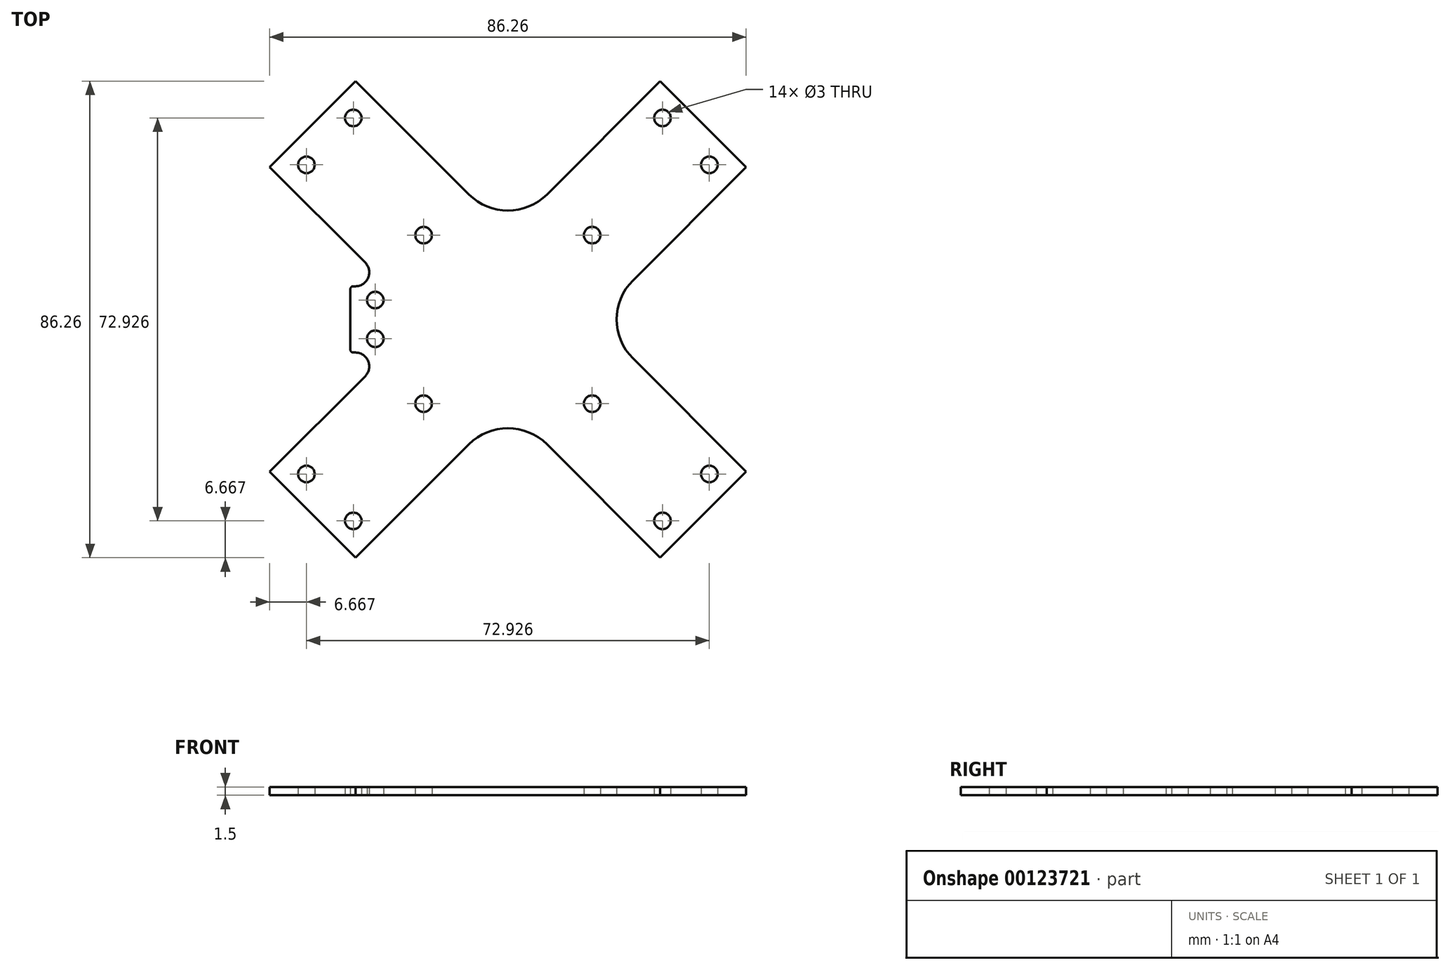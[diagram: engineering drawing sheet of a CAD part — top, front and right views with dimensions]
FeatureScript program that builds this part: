
annotation { "Feature Type Name" : "Feature", "Feature Type Description" : "" }
export const myFeature = defineFeature(function(context is Context, id is Id, definition is map)
    precondition{}
    {
        {
            var Q0;
            Q0=qCreatedBy(makeId("Top.planeOp"),FACE);
            var sketch = newSketch(context, id + "F0", { "sketchPlane" : qUnion([Q0])});
            skLineSegment(sketch, "E0", {"start": v(-42.43, -42.43) * mm, "end": v(42.43, 42.43) * mm, "construction": true});
            skLineSegment(sketch, "E1", {"start": v(-42.43, 42.43) * mm, "end": v(42.43, -42.43) * mm, "construction": true});
            skCircle(sketch, "E2", {"center": v(-15.25, 15.25) * mm, "radius": 1.5 * mm});
            skCircle(sketch, "E3.0.1.0", {"center": v(-15.25, -15.25) * mm, "radius": 1.5 * mm});
            skCircle(sketch, "E3.1.0.0", {"center": v(15.25, 15.25) * mm, "radius": 1.5 * mm});
            skCircle(sketch, "E3.1.1.0", {"center": v(15.25, -15.25) * mm, "radius": 1.5 * mm});
            skLineSegment(sketch, "E3.1.1.1", {"start": v(14.19, -14.19) * mm, "end": v(72.93, -72.93) * mm, "construction": true});
            skLineSegment(sketch, "E3.direction1", {"start": v(-15.25, 15.25) * mm, "end": v(15.25, 15.25) * mm, "construction": true});
            skLineSegment(sketch, "E3.direction2", {"start": v(-15.25, 15.25) * mm, "end": v(-15.25, -15.25) * mm, "construction": true});
            skLineSegment(sketch, "E4", {"start": v(-36.46, 27.98) * mm, "end": v(-27.98, 36.46) * mm, "construction": true});
            skLineSegment(sketch, "E5", {"start": v(27.98, 36.46) * mm, "end": v(36.46, 27.98) * mm, "construction": true});
            skLineSegment(sketch, "E6", {"start": v(27.98, -36.46) * mm, "end": v(36.46, -27.98) * mm, "construction": true});
            skLineSegment(sketch, "E7", {"start": v(-36.46, -27.98) * mm, "end": v(-27.98, -36.46) * mm, "construction": true});
            skCircle(sketch, "E8", {"center": v(-36.46, 27.98) * mm, "radius": 1.5 * mm});
            skCircle(sketch, "E9", {"center": v(-27.98, 36.46) * mm, "radius": 1.5 * mm});
            skCircle(sketch, "E10", {"center": v(27.98, 36.46) * mm, "radius": 1.5 * mm});
            skCircle(sketch, "E11", {"center": v(36.46, 27.98) * mm, "radius": 1.5 * mm});
            skCircle(sketch, "E12", {"center": v(36.46, -27.98) * mm, "radius": 1.5 * mm});
            skCircle(sketch, "E13", {"center": v(27.98, -36.46) * mm, "radius": 1.5 * mm});
            skCircle(sketch, "E14", {"center": v(-27.98, -36.46) * mm, "radius": 1.5 * mm});
            skCircle(sketch, "E15", {"center": v(-36.46, -27.98) * mm, "radius": 1.5 * mm});
            skLineSegment(sketch, "E16", {"start": v(-43.13, 27.58) * mm, "end": v(-27.58, 43.13) * mm});
            skLineSegment(sketch, "E17", {"start": v(27.58, 43.13) * mm, "end": v(43.13, 27.58) * mm});
            skLineSegment(sketch, "E18", {"start": v(27.58, -43.13) * mm, "end": v(43.13, -27.58) * mm});
            skLineSegment(sketch, "E19", {"start": v(-43.13, -27.58) * mm, "end": v(-27.58, -43.13) * mm});
            skPoint(sketch, "E20.endSnap0", {"position": v(-15.25, 0) * mm});
            skLineSegment(sketch, "E21", {"start": v(-43.13, 27.58) * mm, "end": v(-25.82, 10.27) * mm});
            skLineSegment(sketch, "E22", {"start": v(-27.58, 43.13) * mm, "end": v(-7.07, 22.63) * mm});
            skLineSegment(sketch, "E23", {"start": v(-43.13, -27.58) * mm, "end": v(-25.82, -10.27) * mm});
            skLineSegment(sketch, "E24", {"start": v(-27.58, -43.13) * mm, "end": v(-7.07, -22.63) * mm});
            skLineSegment(sketch, "E25.trimOffspring", {"start": v(7.07, -22.63) * mm, "end": v(27.58, -43.13) * mm});
            skLineSegment(sketch, "E26.trimOffspring", {"start": v(22.63, 7.07) * mm, "end": v(43.13, 27.58) * mm});
            skLineSegment(sketch, "E27.trimOffspring", {"start": v(22.63, -7.07) * mm, "end": v(43.13, -27.58) * mm});
            skArc(sketch, "E28", {"start": v(-7.07, 22.63) * mm, "mid": v(0, 19.7) * mm, "end": v(7.07, 22.63) * mm});
            skArc(sketch, "E29", {"start": v(7.07, -22.63) * mm, "mid": v(0, -19.7) * mm, "end": v(-7.07, -22.63) * mm});
            skArc(sketch, "E30", {"start": v(22.63, 7.07) * mm, "mid": v(19.7, 0) * mm, "end": v(22.63, -7.07) * mm});
            skLineSegment(sketch, "E31.trimOffspring", {"start": v(7.07, 22.63) * mm, "end": v(27.58, 43.13) * mm});
            skPoint(sketch, "E32.orphan", {"position": v(-11.93, 11.93) * mm});
            skLineSegment(sketch, "E33", {"start": v(-28.5, 5.5) * mm, "end": v(-28.5, -5.5) * mm});
            skLineSegment(sketch, "E34", {"start": v(-28, -6) * mm, "end": v(-27.6, -6) * mm});
            skLineSegment(sketch, "E35", {"start": v(-28, 6) * mm, "end": v(-27.6, 6) * mm});
            skArc(sketch, "E36", {"start": v(-27.6, 6) * mm, "mid": v(-25.28, 7.54) * mm, "end": v(-25.82, 10.27) * mm});
            skArc(sketch, "E37", {"start": v(-25.82, -10.27) * mm, "mid": v(-25.28, -7.54) * mm, "end": v(-27.6, -6) * mm});
            skArc(sketch, "E38", {"start": v(-28.5, -5.5) * mm, "mid": v(-28.35, -5.85) * mm, "end": v(-28, -6) * mm});
            skArc(sketch, "E39", {"start": v(-28, 6) * mm, "mid": v(-28.35, 5.85) * mm, "end": v(-28.5, 5.5) * mm});
            skLineSegment(sketch, "E40", {"start": v(-24, 3.5) * mm, "end": v(-24, -3.5) * mm, "construction": true});
            skCircle(sketch, "E41", {"center": v(-24, 3.5) * mm, "radius": 1.5 * mm});
            skCircle(sketch, "E42", {"center": v(-24, -3.5) * mm, "radius": 1.5 * mm});
            skSolve(sketch);
        }
        {
            var Q0;
            Q0=qSketchRegion(id+"F0",true);
            extrude(context, id + "F1", {"entities" : qUnion([Q0]), "depth" : 1.5 * mm});
        }
    });
